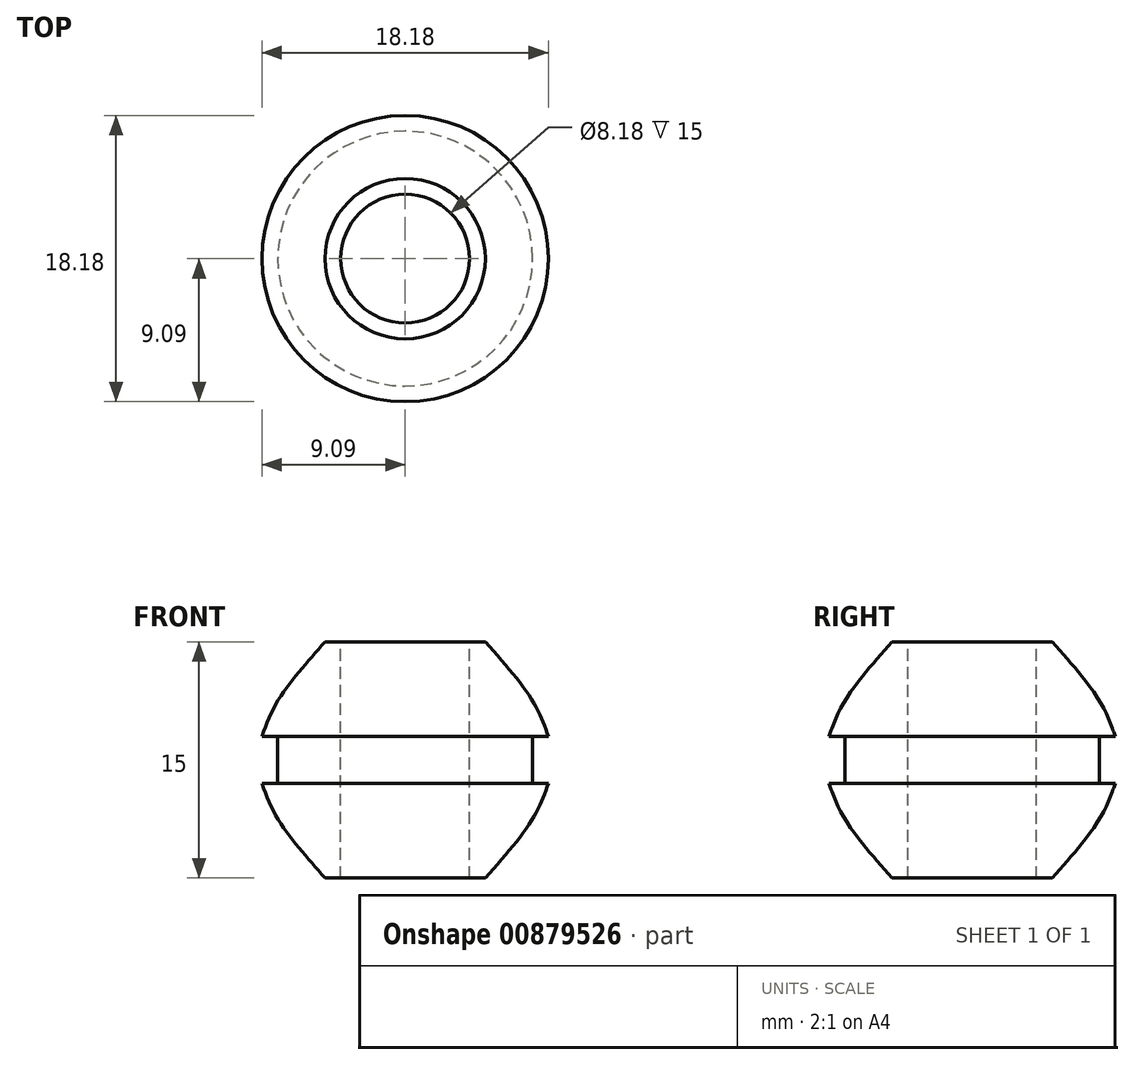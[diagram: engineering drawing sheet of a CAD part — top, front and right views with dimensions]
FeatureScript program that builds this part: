
annotation { "Feature Type Name" : "Feature", "Feature Type Description" : "" }
export const myFeature = defineFeature(function(context is Context, id is Id, definition is map)
    precondition{}
    {
        {
            var Q0;
            Q0=qCreatedBy(makeId("Front.planeOp"),FACE);
            var sketch = newSketch(context, id + "F0", { "sketchPlane" : qUnion([Q0])});
            skLineSegment(sketch, "E0", {"start": v(-4.1, 7.5) * mm, "end": v(-4.1, -7.5) * mm});
            skLineSegment(sketch, "E1", {"start": v(-4.1, 7.5) * mm, "end": v(-5.1, 7.5) * mm});
            skLineSegment(sketch, "E2", {"start": v(-4.1, -7.5) * mm, "end": v(-5.1, -7.5) * mm});
            skLineSegment(sketch, "E3", {"start": v(0, 7.5) * mm, "end": v(0, -7.5) * mm});
            skLineSegment(sketch, "E4", {"start": v(-9.1, 1.5) * mm, "end": v(-8.1, 1.5) * mm});
            skLineSegment(sketch, "E5", {"start": v(-9.1, -1.5) * mm, "end": v(-8.1, -1.5) * mm});
            skLineSegment(sketch, "E6", {"start": v(-8.1, 1.5) * mm, "end": v(-8.1, -1.5) * mm});
            skFitSpline(sketch, "E7", {"points": [v(-5.1, 7.5) * mm, v(-8.1, 3.75) * mm, v(-9.1, 1.5) * mm], "startDerivative": vector(-5.95, -6.74) * mm, "endDerivative": vector(-1.82, -5.17) * mm});
            skFitSpline(sketch, "E8", {"points": [v(-5.1, -7.5) * mm, v(-8.1, -3.75) * mm, v(-9.1, -1.5) * mm], "startDerivative": vector(-5.95, 6.74) * mm, "endDerivative": vector(-1.82, 5.17) * mm});
            skSolve(sketch);
        }
        {
            var Q0;
            Q0=makeQuery(id+"F0.imprint","IMPRINT",FACE,{"disambiguationData":[TD([[makeQuery(id+"F0.imprint","IMPRINT",EDGE,{"derivedFrom":sQuery(id+"F0.wireOp",EDGE,"E0")}),-1.0]])]});
            var Q1;
            Q1=sQuery(id+"F0.wireOp",EDGE,"E3");
            revolve(context, id + "F1", {"surfaceOperationType" : NewSurfaceOperationType.NEW, "entities" : qUnion([Q0]), "axis" : qUnion([Q1]), "revolveType" : RevolveType.FULL});
        }
    });
